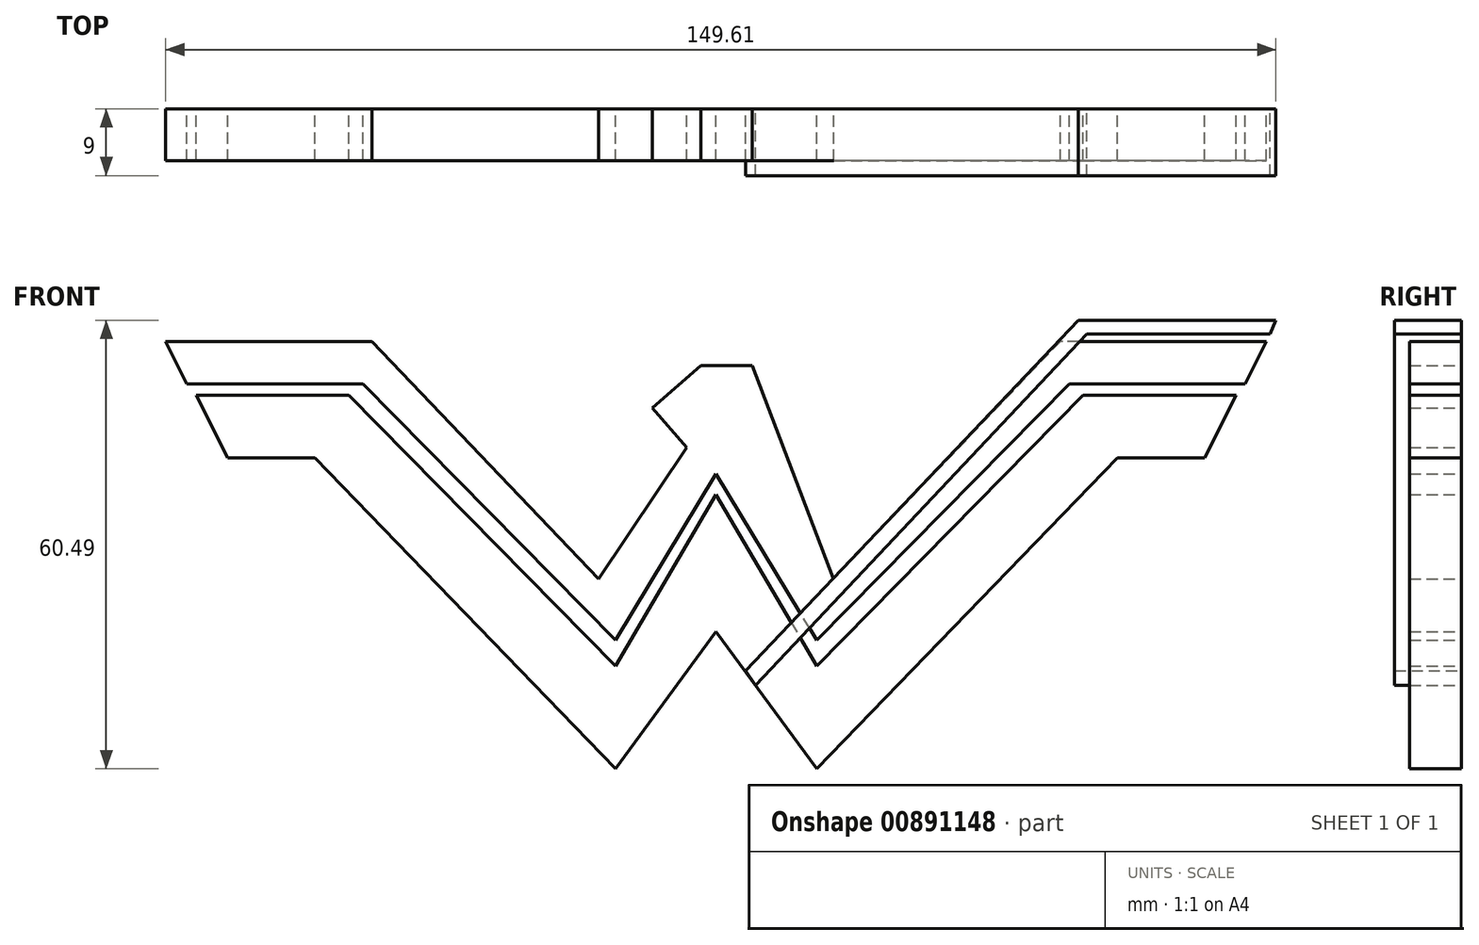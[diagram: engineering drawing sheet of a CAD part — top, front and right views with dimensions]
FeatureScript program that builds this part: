
annotation { "Feature Type Name" : "Feature", "Feature Type Description" : "" }
export const myFeature = defineFeature(function(context is Context, id is Id, definition is map)
    precondition{}
    {
        {
            var Q0;
            Q0=qCreatedBy(makeId("Front.planeOp"),FACE);
            var sketch = newSketch(context, id + "F0", { "sketchPlane" : qUnion([Q0])});
            skLineSegment(sketch, "E0", {"start": v(0, -13.38) * mm, "end": v(-13.58, -36.48) * mm});
            skLineSegment(sketch, "E1", {"start": v(-13.58, -36.48) * mm, "end": v(-49.47, 0) * mm});
            skLineSegment(sketch, "E2", {"start": v(-49.47, 0) * mm, "end": v(-70.08, 0) * mm});
            skLineSegment(sketch, "E3", {"start": v(-70.08, 0) * mm, "end": v(-65.82, -8.4) * mm});
            skLineSegment(sketch, "E4", {"start": v(-65.82, -8.4) * mm, "end": v(-54.09, -8.4) * mm});
            skLineSegment(sketch, "E5", {"start": v(-54.09, -8.4) * mm, "end": v(-13.58, -50.34) * mm});
            skLineSegment(sketch, "E6", {"start": v(-13.58, -50.34) * mm, "end": v(0, -31.86) * mm});
            skLineSegment(sketch, "E7.MirrorCS", {"start": v(0, -13.38) * mm, "end": v(13.58, -36.48) * mm});
            skLineSegment(sketch, "E8.MirrorCS", {"start": v(13.58, -36.48) * mm, "end": v(49.47, 0) * mm});
            skLineSegment(sketch, "E9.MirrorCS", {"start": v(54.09, -8.4) * mm, "end": v(13.58, -50.34) * mm});
            skLineSegment(sketch, "E10.MirrorCS", {"start": v(13.58, -50.34) * mm, "end": v(0, -31.86) * mm});
            skLineSegment(sketch, "E11.MirrorCS", {"start": v(65.82, -8.4) * mm, "end": v(54.09, -8.4) * mm});
            skLineSegment(sketch, "E12.MirrorCS", {"start": v(70.08, 0) * mm, "end": v(65.82, -8.4) * mm});
            skLineSegment(sketch, "E13.MirrorCS", {"start": v(49.47, 0) * mm, "end": v(70.08, 0) * mm});
            skPoint(sketch, "E14.end.orphan", {"position": v(-49.47, 13.27) * mm});
            skPoint(sketch, "E14.start.orphan", {"position": v(-70.08, 13.27) * mm});
            skPoint(sketch, "E15.end.orphan", {"position": v(-49.47, 5.46) * mm});
            skPoint(sketch, "E15.start.orphan", {"position": v(-70.08, 5.46) * mm});
            skLineSegment(sketch, "E16", {"start": v(-71.3, 1.56) * mm, "end": v(-47.59, 1.56) * mm});
            skLineSegment(sketch, "E17", {"start": v(-47.59, 1.56) * mm, "end": v(-13.58, -33) * mm});
            skLineSegment(sketch, "E18", {"start": v(-13.58, -33) * mm, "end": v(0, -10.57) * mm});
            skLineSegment(sketch, "E19", {"start": v(-71.3, 1.56) * mm, "end": v(-74.17, 7.28) * mm});
            skLineSegment(sketch, "E20", {"start": v(-74.17, 7.28) * mm, "end": v(-46.36, 7.28) * mm});
            skLineSegment(sketch, "E21", {"start": v(-46.36, 7.28) * mm, "end": v(-15.83, -24.75) * mm});
            skLineSegment(sketch, "E22", {"start": v(-15.83, -24.75) * mm, "end": v(-3.98, -7.03) * mm});
            skPoint(sketch, "E23.end.orphan", {"position": v(-13.1, 0) * mm});
            skLineSegment(sketch, "E24", {"start": v(-3.98, -7.03) * mm, "end": v(-8.6, -1.71) * mm});
            skLineSegment(sketch, "E25", {"start": v(-8.6, -1.71) * mm, "end": v(-2.04, 4.02) * mm});
            skLineSegment(sketch, "E26", {"start": v(-2.04, 4.02) * mm, "end": v(4.88, 4.02) * mm});
            skLineSegment(sketch, "E27.MirrorCS", {"start": v(13.58, -33) * mm, "end": v(0, -10.57) * mm});
            skLineSegment(sketch, "E28.MirrorCS", {"start": v(47.59, 1.56) * mm, "end": v(13.58, -33) * mm});
            skLineSegment(sketch, "E29.MirrorCS", {"start": v(71.3, 1.56) * mm, "end": v(47.59, 1.56) * mm});
            skLineSegment(sketch, "E30", {"start": v(4.88, 4.02) * mm, "end": v(15.83, -24.75) * mm});
            skPoint(sketch, "E31.end.orphan", {"position": v(-49.47, 12.78) * mm});
            skLineSegment(sketch, "E32", {"start": v(-4.37, -37.8) * mm, "end": v(-6.79, -41.1) * mm});
            skLineSegment(sketch, "E33.MirrorCS", {"start": v(75.27, 8.84) * mm, "end": v(77.17, 12.78) * mm});
            skPoint(sketch, "E34.end.orphan", {"position": v(-45.27, 12.78) * mm});
            skPoint(sketch, "E35.end.orphan", {"position": v(-77.17, 12.78) * mm});
            skPoint(sketch, "E35.start.orphan", {"position": v(-75.27, 8.84) * mm});
            skPoint(sketch, "E36.orphan", {"position": v(-46.36, 8.84) * mm});
            skPoint(sketch, "E37.orphan", {"position": v(4.37, -37.8) * mm});
            skPoint(sketch, "E38.orphan", {"position": v(6.79, -41.1) * mm});
            skPoint(sketch, "E39.orphan", {"position": v(46.36, 8.84) * mm});
            skPoint(sketch, "E40.MirrorCS.start.orphan", {"position": v(75.27, 8.84) * mm});
            skPoint(sketch, "E41.MirrorCS.start.orphan", {"position": v(45.27, 12.78) * mm});
            skPoint(sketch, "E42.MirrorCS.start.orphan", {"position": v(77.17, 12.78) * mm});
            skPoint(sketch, "E43.MirrorCS.end.orphan", {"position": v(46.36, 7.28) * mm});
            skPoint(sketch, "E43.MirrorCS.start.orphan", {"position": v(74.17, 7.28) * mm});
            skPoint(sketch, "E44.MirrorCS.start.orphan", {"position": v(71.3, 1.56) * mm});
            skLineSegment(sketch, "E45.MirrorCS", {"start": v(74.17, 7.28) * mm, "end": v(46.36, 7.28) * mm});
            skLineSegment(sketch, "E46.MirrorCS", {"start": v(71.3, 1.56) * mm, "end": v(74.17, 7.28) * mm});
            skPoint(sketch, "E47.MirrorCS.end.orphan", {"position": v(3.98, -7.03) * mm});
            skPoint(sketch, "E47.MirrorCS.start.orphan", {"position": v(15.83, -24.75) * mm});
            skLineSegment(sketch, "E48.MirrorCS", {"start": v(46.36, 7.28) * mm, "end": v(15.83, -24.75) * mm});
            skSolve(sketch);
        }
        {
            var Q0;
            Q0=qCreatedBy(makeId("Front.planeOp"),FACE);
            var sketch = newSketch(context, id + "F1", { "sketchPlane" : qUnion([Q0])});
            skLineSegment(sketch, "E49", {"start": v(-74.67, 8.25) * mm, "end": v(-49.94, 8.25) * mm});
            skLineSegment(sketch, "E50", {"start": v(-49.94, 8.25) * mm, "end": v(-74.67, 8.25) * mm});
            skLineSegment(sketch, "E51", {"start": v(-74.67, 8.25) * mm, "end": v(-75.44, 10.15) * mm});
            skLineSegment(sketch, "E52", {"start": v(-75.44, 10.15) * mm, "end": v(-48.81, 10.15) * mm});
            skLineSegment(sketch, "E53", {"start": v(-49.94, 8.25) * mm, "end": v(-5.34, -39.08) * mm});
            skLineSegment(sketch, "E54", {"start": v(-48.81, 10.15) * mm, "end": v(-3.98, -37.13) * mm});
            skLineSegment(sketch, "E55", {"start": v(-3.98, -37.13) * mm, "end": v(-5.34, -39.08) * mm});
            skLineSegment(sketch, "E56.MirrorCS", {"start": v(48.81, 10.15) * mm, "end": v(3.98, -37.13) * mm});
            skLineSegment(sketch, "E57.MirrorCS", {"start": v(49.94, 8.25) * mm, "end": v(5.34, -39.08) * mm});
            skLineSegment(sketch, "E58.MirrorCS", {"start": v(3.98, -37.13) * mm, "end": v(5.34, -39.08) * mm});
            skLineSegment(sketch, "E59.MirrorCS", {"start": v(75.44, 10.15) * mm, "end": v(48.81, 10.15) * mm});
            skLineSegment(sketch, "E60.MirrorCS", {"start": v(74.67, 8.25) * mm, "end": v(75.44, 10.15) * mm});
            skLineSegment(sketch, "E61.MirrorCS", {"start": v(49.94, 8.25) * mm, "end": v(74.67, 8.25) * mm});
            skSolve(sketch);
        }
        {
            var Q0;
            Q0=makeQuery(id+"F1.imprint","IMPRINT",FACE,{"disambiguationData":[TD([[makeQuery(id+"F1.imprint","IMPRINT",EDGE,{"derivedFrom":sQuery(id+"F1.wireOp",EDGE,"E50")}),-1.0]])]});
            var Q1;
            Q1=makeQuery(id+"F1.imprint","IMPRINT",FACE,{"disambiguationData":[TD([[makeQuery(id+"F1.imprint","IMPRINT",EDGE,{"derivedFrom":sQuery(id+"F1.wireOp",EDGE,"E56.MirrorCS")}),1.0]])]});
            extrude(context, id + "F2", {"entities" : qUnion([Q0, Q1]), "depth" : 9 * mm, "offsetDistance" : 25 * mm});
        }
        {
            var Q0;
            Q0=makeQuery(id+"F0.imprint","IMPRINT",FACE,{"disambiguationData":[TD([[makeQuery(id+"F0.imprint","IMPRINT",EDGE,{"derivedFrom":sQuery(id+"F0.wireOp",EDGE,"E16")}),1.0]])]});
            var Q1;
            Q1=makeQuery(id+"F0.imprint","IMPRINT",FACE,{"disambiguationData":[TD([[makeQuery(id+"F0.imprint","IMPRINT",EDGE,{"derivedFrom":sQuery(id+"F0.wireOp",EDGE,"E0")}),1.0]])]});
            extrude(context, id + "F3", {"entities" : qUnion([Q0, Q1]), "depth" : 7 * mm, "offsetDistance" : 25 * mm});
        }
    });
